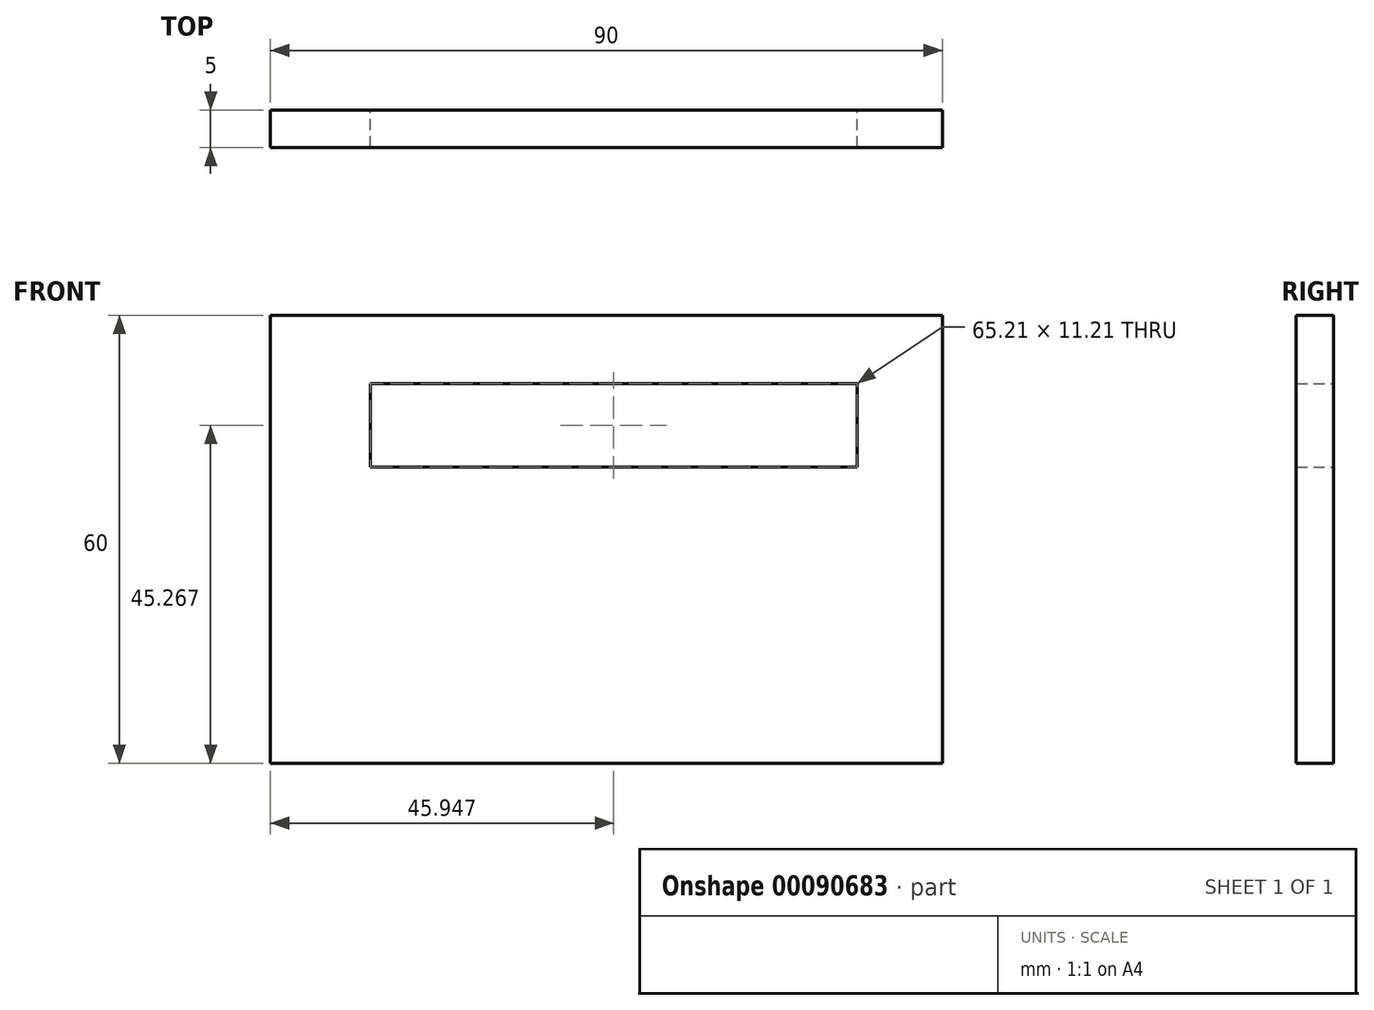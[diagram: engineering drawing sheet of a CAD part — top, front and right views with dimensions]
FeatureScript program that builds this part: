
annotation { "Feature Type Name" : "Feature", "Feature Type Description" : "" }
export const myFeature = defineFeature(function(context is Context, id is Id, definition is map)
    precondition{}
    {
        {
            var Q0;
            Q0=qCreatedBy(makeId("Front.planeOp"),FACE);
            var sketch = newSketch(context, id + "F0", { "sketchPlane" : qUnion([Q0])});
            skLineSegment(sketch, "E0.bottom", {"start": v(-43.12, 20.34) * mm, "end": v(46.88, 20.34) * mm});
            skLineSegment(sketch, "E0.top", {"start": v(-43.12, -39.66) * mm, "end": v(46.88, -39.66) * mm});
            skLineSegment(sketch, "E0.left", {"start": v(-43.12, 20.34) * mm, "end": v(-43.12, -39.66) * mm});
            skLineSegment(sketch, "E0.right", {"start": v(46.88, 20.34) * mm, "end": v(46.88, -39.66) * mm});
            skLineSegment(sketch, "E1.bottom", {"start": v(-29.78, 11.21) * mm, "end": v(35.43, 11.21) * mm});
            skLineSegment(sketch, "E1.top", {"start": v(-29.78, 0) * mm, "end": v(35.43, 0) * mm});
            skLineSegment(sketch, "E1.left", {"start": v(-29.78, 11.21) * mm, "end": v(-29.78, 0) * mm});
            skLineSegment(sketch, "E1.right", {"start": v(35.43, 11.21) * mm, "end": v(35.43, 0) * mm});
            skSolve(sketch);
        }
        {
            var Q0;
            Q0=makeQuery(id+"F0.imprint","IMPRINT",FACE,{"disambiguationData":[TD([[makeQuery(id+"F0.imprint","IMPRINT",EDGE,{"derivedFrom":sQuery(id+"F0.wireOp",EDGE,"E0.bottom")}),-1.0]])]});
            extrude(context, id + "F1", {"entities" : qUnion([Q0]), "depth" : 5 * mm});
        }
    });
